# Revit family: Maxlogic Contrôle Panneaux d'Alarme Incendie Conventionnelle grande caisse
name_source: partatom
category: Fire Alarm Devices
units: mm (PartAtom-declared; Revit-internal decimal feet)

## family parameters
Cut with Voids When Loaded = No
Host = Face
Maintain Annotation Orientation = Yes
OmniClass Number = 23.85.30.21
OmniClass Title = Environmental Detection/Registration
Part Type = Normal
Room Calculation Point = No
Round Connector Dimension = Use Diameter
Shared = No

## types (4) — shared parameters
Adresse ligne 1 = Şerifali Mahallesi Kutup Sokak No:27/1-2-4 Ümraniye TR-34775 İSTANBUL
Alimentation d'externe = 220 V AC
Batterie = 2 X (12V DC 7 Ah )
Code de  Performance = EN 54-2 / EN 54-4
Couleur = Blanc
Deuxime Matèriel = Plastique Blanche ABS
Durée de la garantie Travail = 2
Durée de la garantie réservé = 2
Hauteur Nominale = 300 mm
Largeur Nominale = 100 mm
Longeur Nominale = 400 mm
Manuel d'installation = https://mavilielektronik.com
Manufacturer = Mavili Elektronik Ticaret A.Ş.
Matériel Principe = Mètale Grise
Model = Maxlogic
Numèro de Fax = (+)90 216 466 45 10
Poids = ~ 4,275 - 4,4 kg (sans batterie)
Surface de Montage = Montage à Mur
Tempèrature de Fonctionnement = (-5°C) - (+50°C)
URL = https://www.mavili.com.tr
Unité de durée de garantie = Ans
zero-valued in all types: Cost, Default Elevation

## per-type parameters (varying)
| type | Code de Produit | Description | LED 2 | LED 4 | LED 8 | Numéro de pose des travaux publics |
| Maxlogic Panneau Contrôle d'Incendie Conventionnelle, 16 Zone | ML-22116 | Panneau Contrôle d'Incendie Conventionnelle, 16 zone | Yes | Yes | Yes | 833-214 |
| Maxlogic Panneau Contrôle d'Incendie Conventionnelle, 8 Zone | ML-22108 | Panneau Contrôle d'Incendie Conventionnelle, 8 Zone | Yes | Yes | No | 833-212 |
| Maxlogic Panneau Contrôle d'Incendie Conventionnelle, 4 Zone | ML-22104 | Panneau Contrôle d'Incendie Conventionnelle , 4 Zone | Yes | No | No | 833-211 |
| Maxlogic Panneau Contrôle d'Incendie Conventionnelle, 2 Zone | ML-22102 | Panneau Contrôle d'Incendie Conventionnelle, 2 Zone | No | No | No |  |

## geometry (parser evidence)
native form markers: Sweep x1
no freeform markers — native parametric forms only
